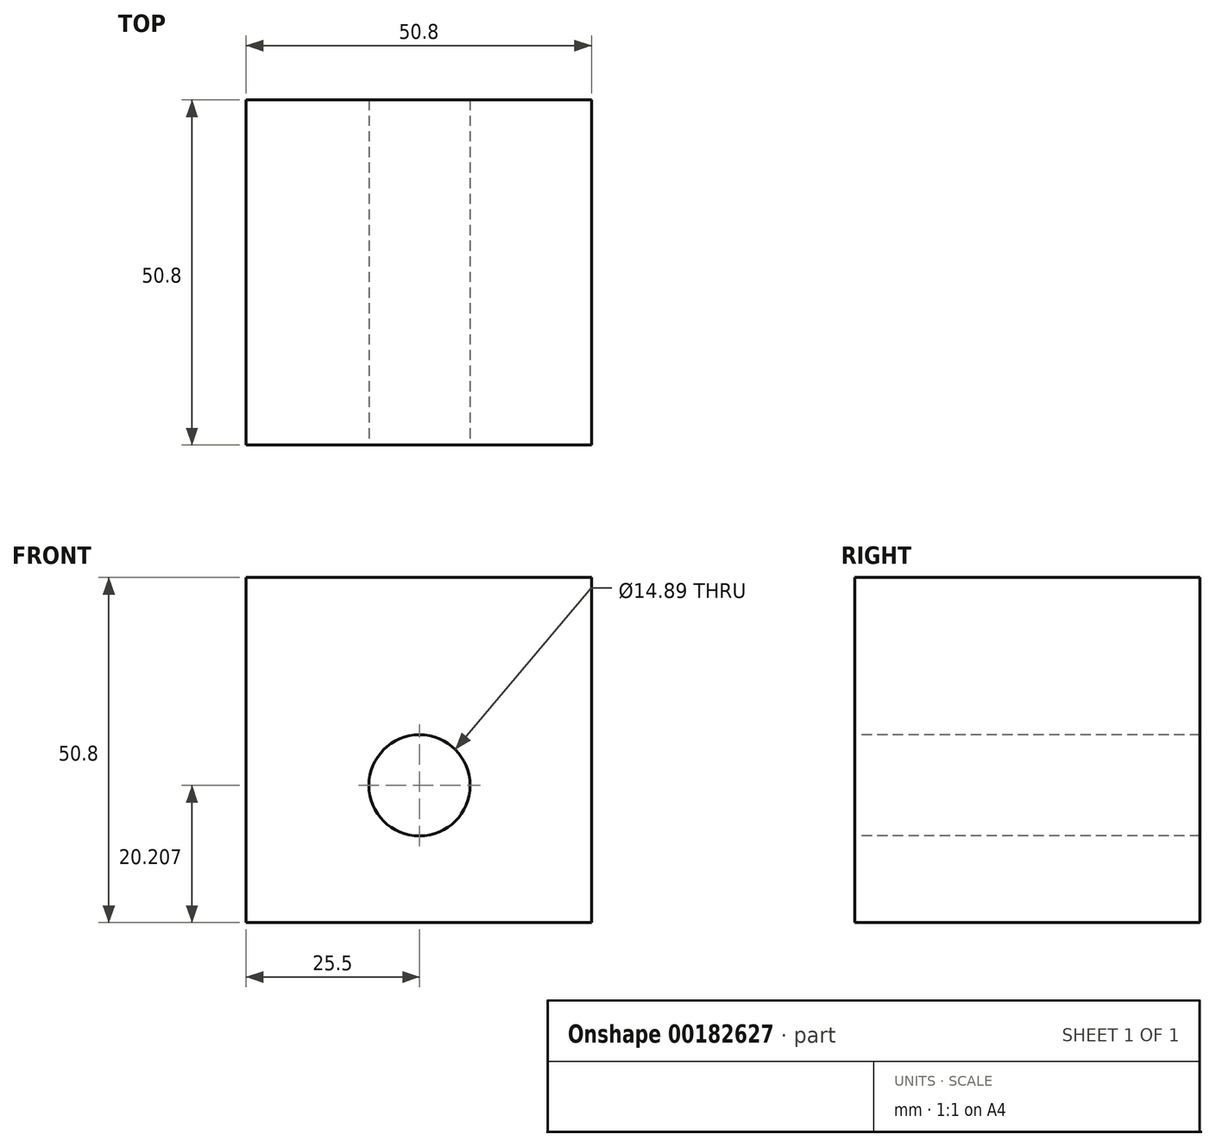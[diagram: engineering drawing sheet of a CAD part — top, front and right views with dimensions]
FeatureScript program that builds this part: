
annotation { "Feature Type Name" : "Feature", "Feature Type Description" : "" }
export const myFeature = defineFeature(function(context is Context, id is Id, definition is map)
    precondition{}
    {
        {
            var Q0;
            Q0=qCreatedBy(makeId("Front.planeOp"),FACE);
            var sketch = newSketch(context, id + "F0", { "sketchPlane" : qUnion([Q0])});
            skLineSegment(sketch, "E0", {"start": v(-25.5, 20.3) * mm, "end": v(-25.5, -30.5) * mm});
            skLineSegment(sketch, "E1", {"start": v(-25.5, -30.5) * mm, "end": v(25.3, -30.5) * mm});
            skLineSegment(sketch, "E2", {"start": v(25.3, -30.5) * mm, "end": v(25.3, 20.3) * mm});
            skLineSegment(sketch, "E3", {"start": v(-25.5, 20.3) * mm, "end": v(25.3, 20.3) * mm});
            skSolve(sketch);
        }
        {
            var Q0;
            Q0=makeQuery(id+"F0.imprint","IMPRINT",FACE,{"disambiguationData":[TD([[makeQuery(id+"F0.imprint","IMPRINT",EDGE,{"derivedFrom":sQuery(id+"F0.wireOp",EDGE,"E0")}),1.0]])]});
            extrude(context, id + "F1", {"entities" : qUnion([Q0]), "depth" : 50.8 * mm});
        }
        {
            var Q0;
            Q0=makeQuery(id+"F1.opExtrude","CAP_FACE",FACE,{"disambiguationData":[OSD([sQuery(id+"F0.wireOp",EDGE,"E0"),sQuery(id+"F0.wireOp",EDGE,"E1"),sQuery(id+"F0.wireOp",EDGE,"E2"),sQuery(id+"F0.wireOp",EDGE,"E3")])],"isStart":false});
            var sketch = newSketch(context, id + "F2", { "sketchPlane" : qUnion([Q0])});
            skCircle(sketch, "E4", {"center": v(0, -10.28) * mm, "radius": 7.45 * mm});
            skSolve(sketch);
        }
        {
            var Q0;
            Q0=makeQuery(id+"F2.imprint","IMPRINT",FACE,{"disambiguationData":[TD([[makeQuery(id+"F2.imprint","IMPRINT",EDGE,{"derivedFrom":sQuery(id+"F2.wireOp",EDGE,"E4")}),1.0]])]});
            extrude(context, id + "F3", {"entities" : qUnion([Q0]), "operationType" : NewBodyOperationType.REMOVE, "oppositeDirection" : true, "depth" : 50.8 * mm});
        }
        {
            var Q0;
            Q0=qCreatedBy(makeId("Top.planeOp"),FACE);
            var sketch = newSketch(context, id + "F4", { "sketchPlane" : qUnion([Q0])});
            skCircle(sketch, "E5.cCircle", {"center": v(-51.97, 55.13) * mm, "radius": 4.76 * mm, "construction": true});
            skLineSegment(sketch, "E5.0", {"start": v(-47.85, 52.74) * mm, "end": v(-51.98, 50.36) * mm});
            skLineSegment(sketch, "E5.1", {"start": v(-51.98, 50.36) * mm, "end": v(-56.1, 52.75) * mm});
            skLineSegment(sketch, "E5.2", {"start": v(-56.1, 52.75) * mm, "end": v(-56.1, 57.51) * mm});
            skLineSegment(sketch, "E5.3", {"start": v(-56.1, 57.51) * mm, "end": v(-51.96, 59.89) * mm});
            skLineSegment(sketch, "E5.4", {"start": v(-51.96, 59.89) * mm, "end": v(-47.84, 57.5) * mm});
            skLineSegment(sketch, "E5.5", {"start": v(-47.84, 57.5) * mm, "end": v(-47.85, 52.74) * mm});
            skSolve(sketch);
        }
        {
            var Q0;
            Q0 = qSketchRegion(id + "F4", true);
            extrude(context, id + "F5", {"entities" : qUnion([Q0]), "depth" : 4.76 * mm});
        }
        {
            var Q0;
            Q0=makeQuery(id+"F4.imprint","IMPRINT",FACE,{"disambiguationData":[TD([[makeQuery(id+"F4.imprint","IMPRINT",EDGE,{"derivedFrom":sQuery(id+"F4.wireOp",EDGE,"E5.0")}),-1.0]])]});
            var sketch = newSketch(context, id + "F6", { "sketchPlane" : qUnion([Q0])});
            skCircle(sketch, "E6", {"center": v(-51.97, 55.13) * mm, "radius": 1.59 * mm});
            skSolve(sketch);
        }
        {
            var Q0;
            Q0=makeQuery(id+"F5.opExtrude","CAP_FACE",FACE,{"disambiguationData":[OSD([sQuery(id+"F4.wireOp",EDGE,"E5.0"),sQuery(id+"F4.wireOp",EDGE,"E5.1"),sQuery(id+"F4.wireOp",EDGE,"E5.2"),sQuery(id+"F4.wireOp",EDGE,"E5.3"),sQuery(id+"F4.wireOp",EDGE,"E5.4"),sQuery(id+"F4.wireOp",EDGE,"E5.5")])],"isStart":false});
            var Q1;
            Q1 = qSketchRegion(id + "F6", true);
            extrude(context, id + "F7", {"entities" : qUnion([Q0, Q1]), "operationType" : NewBodyOperationType.REMOVE, "oppositeDirection" : true, "depth" : 25.4 * mm});
        }
    });
